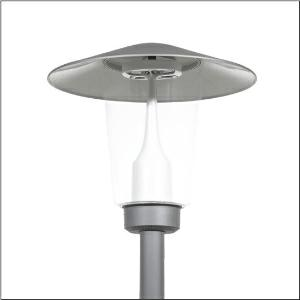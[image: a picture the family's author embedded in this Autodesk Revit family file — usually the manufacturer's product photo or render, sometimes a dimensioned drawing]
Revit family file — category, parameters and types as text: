
# Revit family: pilzleuchte_iq___st1_2a_5xa5235ef14hp_2efb
name_source: partatom
category: Lighting Fixtures
units: mm (PartAtom-declared; Revit-internal decimal feet)

## family parameters
Cut with Voids When Loaded = No
Host = Face
Light Source = No
Part Type = Normal
Room Calculation Point = No
Round Connector Dimension = Use Diameter
Shared = No

## types (1)
- --- (1 x LED, 4770 lm, 33.6 W, 3000K)
    Apparent Load = 34 VA
    CIE Flux Codes = 23 60 92 98 100
    Color Rendering = 70
    Color Temperature = 3000K
    Default Elevation = 1800 mm
    Description = Mushroom Luminaire iQ, mast luminaire, Module 540 iQ-SR, primary light control with 3 zone facetted reflector, of plastic, silver coated, highly specular, structured, primary optical cover: cover, of PMMA, transparent, light distribution: ST1.2a, light emission: direct distribution, primary light characteristic: asymmetric, installation type: post-top, LED, High Power LED, rated luminous flux: 4.770lm, luminous efficacy: 142lm/W, light colour: 730, colour temperature: 3000K, control gear: ECG iQ, control: pre-setting: logarithmic dimming characteristic, Street-Remote, Auto-Match, Temp-Guard, Lumen-Switch, Night-Set, Smart-Wire, Light-Fading, Desk-Remote (wireless, voltage-free reading and setting of iQ features in the workshop via application-optimized NFC function/RFID function), optimised constant luminous flux control (CLO 2.0), with terminal, 6-pole, max. 2.5mm², mains connection: 230..240V, AC, 50/60Hz, start of lifetime: 34W, end of service life: 36W, reduction: 15W, luminaire housing, upper part, of glass-fibre reinforced polyester, coated, Siteco® metallic grey (DB 702S), diameter: 650mm, height: 586mm, spigot size: d x l = 76 x 70mm (post-top) | with reducer (optional accessory) 60 x 70mm, post-top mast mounting element, of diecast aluminium, coated, Siteco® metallic grey (DB 702S), Module 540 iQ-SR, traffic white (RAL 9016), equipment: Power, protection rating (complete): IP65, insulation class (complete): insulation class II (safety insulation), certification: CE, ENEC, VDE, packaging unit: 1 piece

Light Distribution: ST1.2a
    Height = 586 mm
    Lamp = 1 x LED
    Lamp Light Flux = 4770 lm
    Lamp Power = 33.6 W
    Lamp count = 1
    Length = 650 mm
    Luminous efficacy = 142 lm/W
    Manufacturer = Siteco
    ModVariant = No
    Model = 5XA5235EF14HP
    Number of Poles = 1
    OnlyDefault = Yes
    Power Factor = 1
    Product Name = Pilzleuchte iQ | ST1.2a
    Product group = mast luminaire | pylon top
    ProductGroupID = 6100
    Protection Class = Protection class II
    Protection Degree = IP 65
    RLX_Detail_Level = 1
    RLX_Emergency_Light_Flux = 0 lm
    RLX_Emergency_Type = 0
    RLX_Emergency_Type_DB = No
    RlxData = <blob elided: 51545 chars, md5=74738d74>
    Socket = socket
    Standby Power = 0 W
    System Light Flux = 4770 lm
    System Power = 34 W
    Type Comments = factory setting: luminous flux: 100 % | dim-lin: 254 | 695 mA
    Type Image = l_1006077.jpg
    URL = http://relux.com
    VarID = @adj_166305
    Voltage = 0 V
    Weight = 0.00 kg
    Width = 0 mm  [stored 0 ft]

note: [stored X ft] marks values corroborated as IEEE doubles in the binary element streams (Revit-internal decimal feet)

## geometry (parser evidence)
native form markers: Blend x4, Sweep x11
no freeform markers — native parametric forms only
